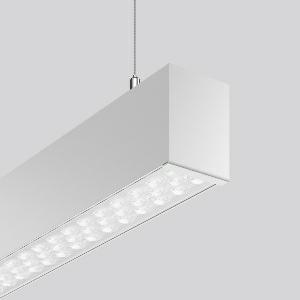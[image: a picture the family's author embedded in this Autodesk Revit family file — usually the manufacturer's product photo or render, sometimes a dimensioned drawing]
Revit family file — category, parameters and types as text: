
# Revit family: linedo_single_ip20_312563_000_9cd5
name_source: partatom
category: Lighting Fixtures
units: mm (PartAtom-declared; Revit-internal decimal feet)

## family parameters
Cut with Voids When Loaded = No
Host = Face
Light Source = No
Part Type = Normal
Room Calculation Point = No
Round Connector Dimension = Use Diameter
Shared = No

## types (1)
- LINEDO single IP20 (1 x LED Modul 830, 4550 lm, 3000)
    Apparent Load = 31 VA
    CIE Flux Codes = 86 96 99 100 100
    Color Rendering = 80
    Color Temperature = 3000
    Default Elevation = 1800 mm
    Description = Series: LINEDO single IP20
Stylish pendant luminaire. Housing: extruded aluminium profile, anodised. End cap aluminium powder-coated, without visible screws. High-efficiency LED units with optimum light control thanks to clear plastic (PC) lens optics. 2-point steel cable suspension freely positionable and infinitely height-adjustable. With power cord (2.5 m). Please order canopy separately if required. Perfect for office areas (RUG < 19) and environments with computer screens in accordance with EN 12464-1. 
Colour: anodised aluminium
Length: 1700 mm
Width: 58 mm
Height: 76 mm
Suspension length: 100-1500 mm
Lamp: LED
Socket: without socket
Colour temperature: 3000K
Colour rendering index (CRI): 80
System power: 31 W
Rated luminous flux: 4550 lm
Beam angle Down: 59°
Luminous efficiency: 147 lm/W
Control gear: Regulated power supply
Protection class: I
Type of protection: IP 20
    Height = 76 mm
    Lamp = 1 x LED Modul 830
    Lamp Light Flux = 4550 lm
    Lamp count = 1
    Length = 1700 mm
    Lifetime = 50000 h
    Luminous efficacy = 147 lm/W
    Manufacturer = RZB
    ModVariant = No
    Model = 312563.000
    Mounting Place = Ceiling
    Mounting Type = Pendant
    Number of Poles = 1
    OnlyDefault = Yes
    Power Factor = 1
    Product Name = LINEDO single IP20
    Product group = Pendant luminaires
    ProductGroupID = 902
    Protection Class = Protection class I
    Protection Degree = Degree of protection
    RLX_Detail_Level = 1
    RLX_Emergency_Light_Flux = 0 lm
    RLX_Emergency_Type = 0
    RLX_Emergency_Type_DB = No
    RlxData = <blob elided: 29341 chars, md5=ac26090e>
    Socket = socket
    Standby Power = 0 W
    System Light Flux = 4550 lm
    System Power = 31 W
    Type Comments = ALEA SPOT
    Type Image = 312563.000.jpg
    URL = http://relux.com
    VarID = ---
    Voltage = 0 V
    Weight = 0.00 kg
    Width = 58 mm

## geometry (parser evidence)
native form markers: Blend x4, Sweep x10
no freeform markers — native parametric forms only
